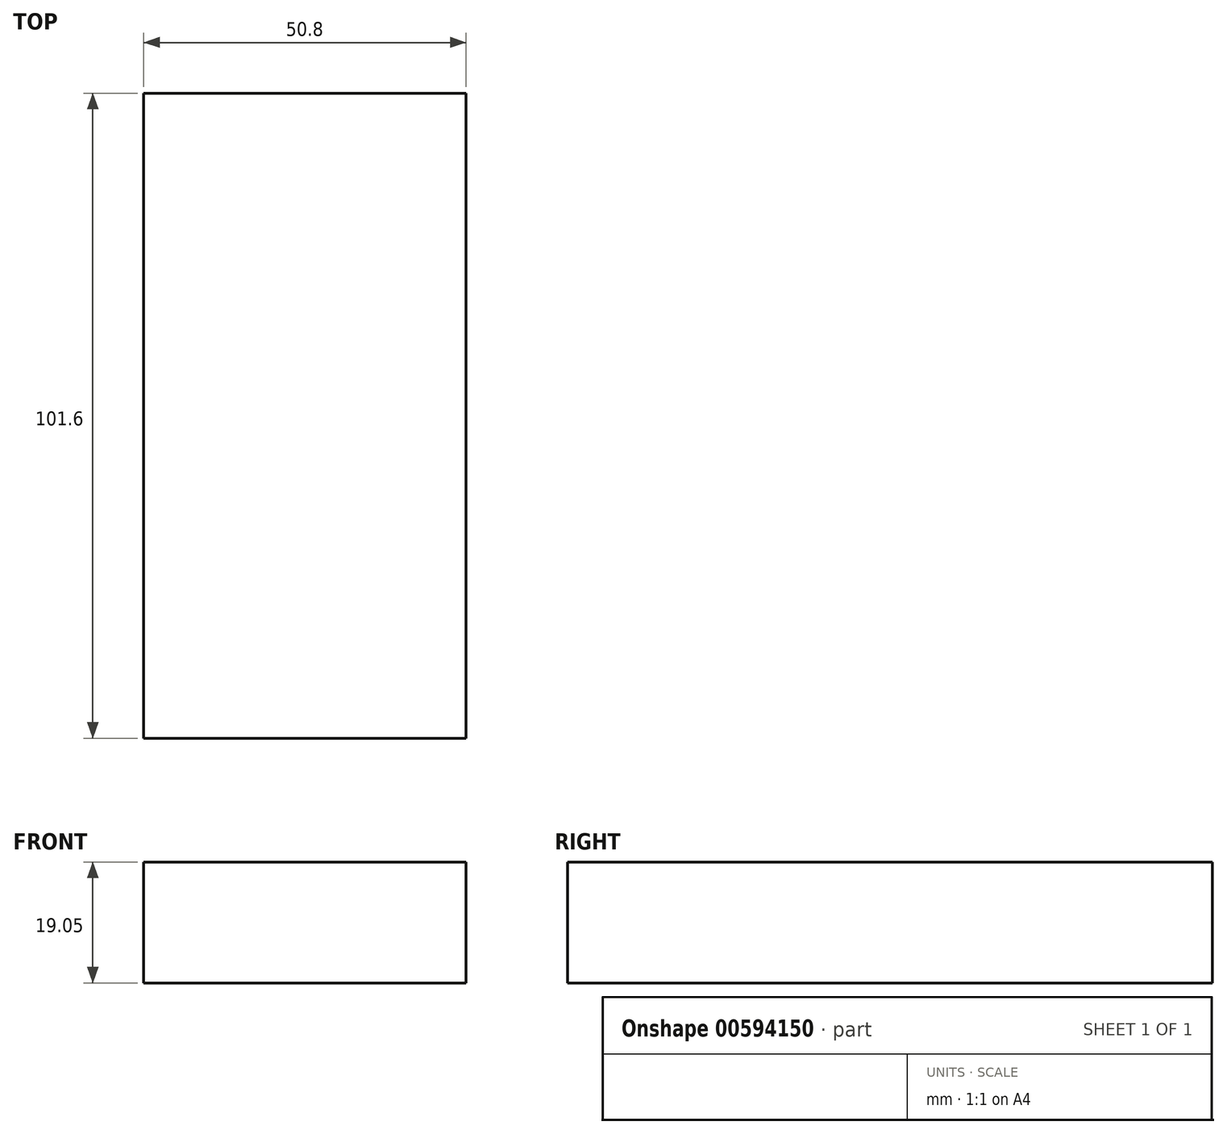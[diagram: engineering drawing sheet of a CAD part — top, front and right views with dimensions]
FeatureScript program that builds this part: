
annotation { "Feature Type Name" : "Feature", "Feature Type Description" : "" }
export const myFeature = defineFeature(function(context is Context, id is Id, definition is map)
    precondition{}
    {
        {
            var Q0;
            Q0=qCreatedBy(makeId("Top.planeOp"),FACE);
            var sketch = newSketch(context, id + "F0", { "sketchPlane" : qUnion([Q0])});
            skLineSegment(sketch, "E0.bottom", {"start": v(-25.4, 50.8) * mm, "end": v(25.4, 50.8) * mm});
            skLineSegment(sketch, "E0.top", {"start": v(-25.4, -50.8) * mm, "end": v(25.4, -50.8) * mm});
            skLineSegment(sketch, "E0.left", {"start": v(-25.4, 50.8) * mm, "end": v(-25.4, -50.8) * mm});
            skLineSegment(sketch, "E0.right", {"start": v(25.4, 50.8) * mm, "end": v(25.4, -50.8) * mm});
            skPoint(sketch, "E0.middle", {"position": v(0, 0) * mm});
            skSolve(sketch);
        }
        {
            var Q0;
            Q0 = qSketchRegion(id + "F0", true);
            extrude(context, id + "F1", {"entities" : qUnion([Q0]), "depth" : 19.05 * mm, "offsetDistance" : 25.4 * mm});
        }
    });
